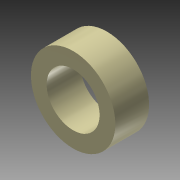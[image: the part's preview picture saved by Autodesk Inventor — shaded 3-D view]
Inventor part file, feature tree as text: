
AUTODESK INVENTOR PART (.ipt)
format: ipt  version: 2014 SP1 (Build 180222100, 222)  size: 84,992 bytes
history: native  units: in
note: dims shown in document units (in); Inventor stores cm internally (conversion verified against a paired STEP export)
features: revolve x1, sketch x1
ambient origin geometry x8: Origin, YZ Plane, XZ Plane, XY Plane, X Axis, Y Axis, Z Axis, Center Point
bodies: Solid1 (feature_tree)
feature tree (2):
  revolve  "Revolution1"  [1 undecoded]
  sketch  "Sketch1"  dims[d0=0.125in d1=0.196in d2=0.3125in d3=90.0deg]
note: 1 required parameter value undecoded (feature->parameter linkage not recoverable at this tier; creation-order binding heuristic only, values carry confidence <= 0.55)
